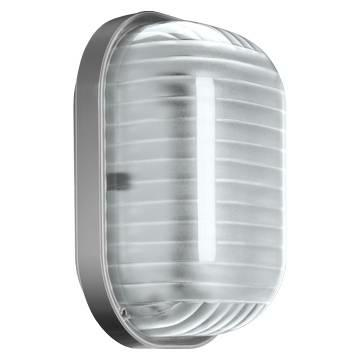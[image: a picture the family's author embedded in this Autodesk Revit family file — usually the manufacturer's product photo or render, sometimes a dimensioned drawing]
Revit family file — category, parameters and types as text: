
# Revit family: Lighting-CommercialSector-GEWISS-GUSCIO-WATERTIGHT-LED_COMPACT_250
name_source: partatom
category: Apparecchi per illuminazione
revit_build: Autodesk Revit 2016 (Build: 20161004_0715(x64)
units: mm (PartAtom-declared; Revit-internal decimal feet)

## family parameters
Condiviso = No
Host = Superficie
Numero OmniClass = 23.80.00.00
Punto di calcolo locali = No
Quota connettore circolare = Usa diametro
Sorgente d'illuminazione = Sì
Taglio con vuoti quando caricato = No
Tipo di parte = Normale
Titolo OmniClass = Electric Power and Lighting

## types (6) — shared parameters
Angolo inclinazione = 0.00°
Application = Indoor / Outdoor
Carico apparente = 9 VA
Catalogue = LIGHTING
Catalogue Range = GUSCIO
Electrocod = 2424
Emetti da lunghezza linea = 610 mm
File diagramma fotometrico = GW80772-80604359.IES
Filtro dei colori = 16777215
GEWISS - LED = GEWISS - Led - lm 650 / Temp_3000_K
GEWISS - STRUTTURA = GEWISS - Grigio Graffite
GEWISS - VETRO = GEWISS - vetro guscio
Glow Wire Test = 850°C
IDF = 564909d3-2cd1-4601-ab12-82b5c35fbf71
IDT = 645e3633-7bed-4783-a402-f8a5d8b31279
IP degree = IP55
Immagine tipo = GW80771.jpg
Insulation class = II
Lampada = FSD
Material = Polycarbonate
Numero di poli = 2
Produttore = GEWISS S.p.A.
Prospetto di default = 1219 mm
Shock resistance = IK10
Technical sheet = https://www.gewiss.com
URL = https://www.gewiss.com
Variazione temperatura colore lampada con luminosità attenuata = <Nessuno>
Version file RFA = 18.0
Voltaggio = 230 V

## per-type parameters (varying)
| type | Colour | Descrizione | Driver type | EAN code | Efficiency class of the lamp supplied | Lamp holder | Lamp power | Modello | Version type | Voltage | Weight (kg) |
| GW80601 - For lamp E27 60W - Grey - IP55 | Grey RAL 7035 | GUSCIO 250x175 60W E27 IP55 GR.RAL7035 |  | 8011564015180 | D ÷ A+ | E27 | 60W | GW80601 | Guscio 250 |  | 0,5 |
| GW80771 - For lamp E27 60W - Grey - IP55 | Graphite grey | GUSCIO 250x175 60W E27 IP55 G.GREY |  | 8011564210509 | D ÷ A+ | E27 | 60W | GW80771 | Guscio 250 |  | 0,5 |
| GW80772 - For lamp FSD 9W - Grey - IP55 | Graphite grey | GUSCIO 250x175 1X9W G23 IP55 G.GREY | KCG electromagnetic reactor | 8011564210516 | B ÷ A | G23 |  | GW80772 | Guscio 250 | 230 V - 50 Hz | 0,9 |
| GW80646 - For lamp FSQ 13W - Grey - IP55 | Grey RAL 7035 | GUSCIO250x175 1x13W G24q-1 IP55 RAL7035 | EVG electronic reactor | 8011564183544 | B ÷ A | G24q-1 |  | GW80646 | Guscio 250 | 230 / 240 V - 50 / 60 Hz | 0,7 |
| GW80644 - For lamp FSD 9W - With photo electric cell - Grey - IP55 | Grey RAL 7035 | GUSCIO250x175 1X9W G23 CREPUSCUL.RAL7035 | KCG electromagnetic reactor | 8011564034723 | B ÷ A | G23 |  | GW80644 | Guscio 250 - With light-sensitive one-way switch | 230 V - 50 Hz | 1 |
| GW80604 - For lamp FSD 9W - Grey - IP55 | Grey RAL 7035 | GUSCIO 250x175 1X9W G23 IP55 GR.RAL7035 | KCG electromagnetic reactor | 8011564015210 | B ÷ A | G23 |  | GW80604 | Guscio 250 | 230 V - 50 Hz | 0,9 |
